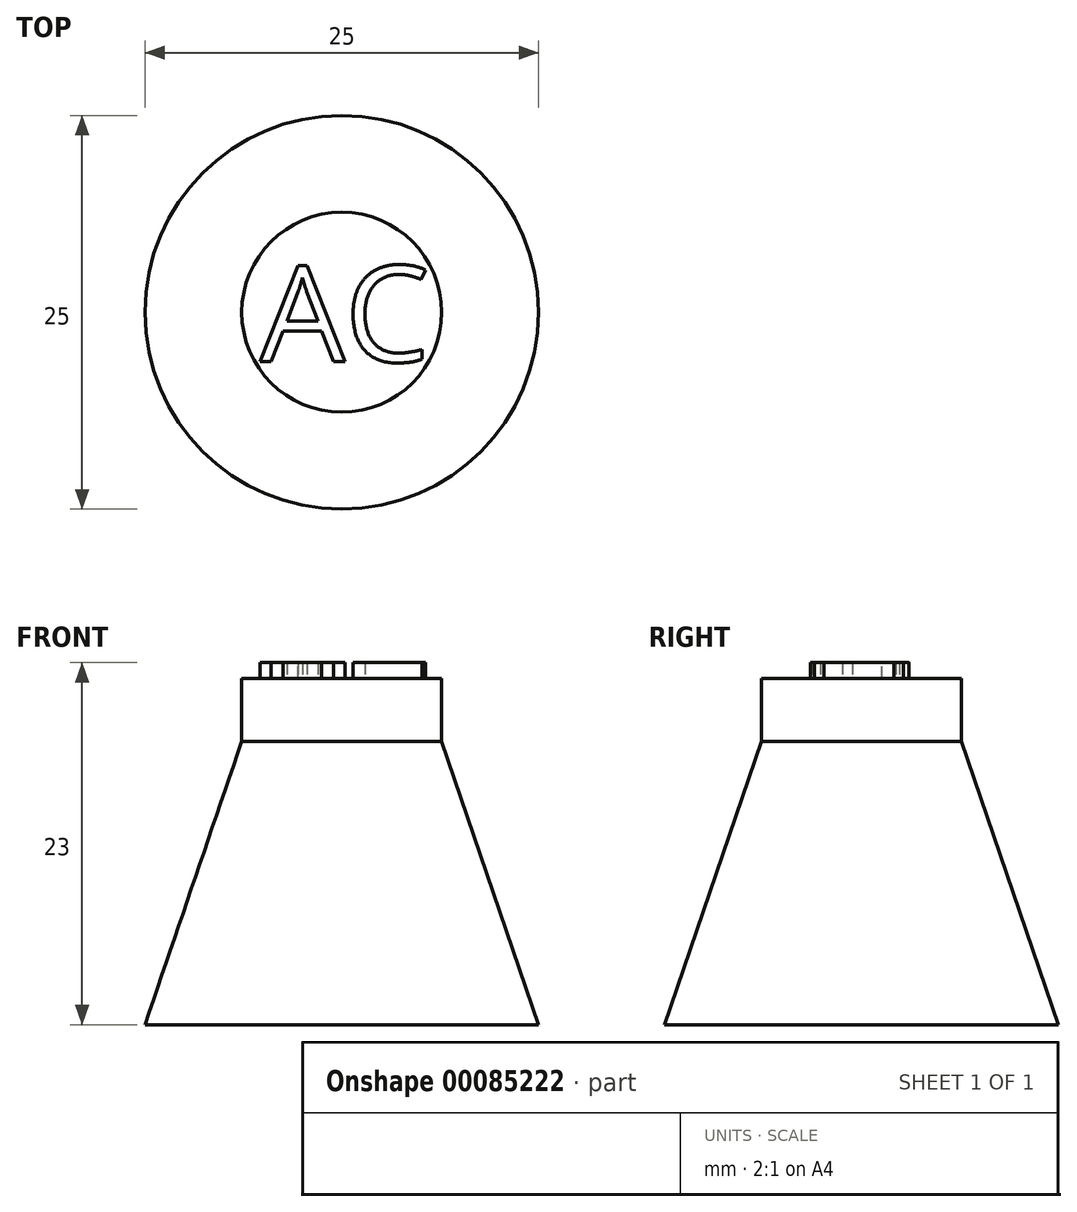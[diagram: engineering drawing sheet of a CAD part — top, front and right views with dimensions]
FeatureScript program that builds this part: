
annotation { "Feature Type Name" : "Feature", "Feature Type Description" : "" }
export const myFeature = defineFeature(function(context is Context, id is Id, definition is map)
    precondition{}
    {
        {
            var Q0;
            Q0=qCreatedBy(makeId("Front.planeOp"),FACE);
            var sketch = newSketch(context, id + "F0", { "sketchPlane" : qUnion([Q0])});
            skLineSegment(sketch, "E0", {"start": v(0, 0) * mm, "end": v(12.5, 0) * mm});
            skLineSegment(sketch, "E1", {"start": v(0, 0) * mm, "end": v(0, 18) * mm});
            skLineSegment(sketch, "E2", {"start": v(0, 18) * mm, "end": v(6.35, 18) * mm});
            skLineSegment(sketch, "E3", {"start": v(6.35, 18) * mm, "end": v(6.35, 22) * mm});
            skLineSegment(sketch, "E4", {"start": v(12.5, 0) * mm, "end": v(6.35, 18) * mm});
            skLineSegment(sketch, "E5", {"start": v(6.35, 22) * mm, "end": v(0, 22) * mm});
            skLineSegment(sketch, "E6", {"start": v(0, 22) * mm, "end": v(0, 18) * mm});
            skLineSegment(sketch, "E7", {"start": v(6.35, 18) * mm, "end": v(4.85, 18) * mm});
            skLineSegment(sketch, "E8", {"start": v(12.5, 0) * mm, "end": v(11, 0) * mm});
            skLineSegment(sketch, "E9", {"start": v(4.85, 18) * mm, "end": v(11, 0) * mm});
            skLineSegment(sketch, "E10", {"start": v(4.85, 18) * mm, "end": v(4.85, 22) * mm});
            skSolve(sketch);
        }
        {
            var Q0;
            Q0=makeQuery(id+"F0.imprint","IMPRINT",FACE,{"disambiguationData":[TD([[makeQuery(id+"F0.imprint","IMPRINT",EDGE,{"derivedFrom":sQuery(id+"F0.wireOp",EDGE,"E2")}),1.0]])]});
            var Q1;
            {var subQ0=sQuery(id+"F0.wireOp",EDGE,"E3");Q1=makeQuery(id+"F0.imprint","IMPRINT",FACE,{"disambiguationData":[TD([[makeQuery(id+"F0.imprint","IMPRINT",EDGE,{"derivedFrom":subQ0}),1.0]])]});}
            var Q2;
            Q2=makeQuery(id+"F0.imprint","IMPRINT",FACE,{"disambiguationData":[TD([[makeQuery(id+"F0.imprint","IMPRINT",EDGE,{"derivedFrom":sQuery(id+"F0.wireOp",EDGE,"E4")}),1.0]])]});
            var Q3;
            Q3=makeQuery(id+"F0.imprint","IMPRINT",FACE,{"disambiguationData":[TD([[makeQuery(id+"F0.imprint","IMPRINT",EDGE,{"derivedFrom":sQuery(id+"F0.wireOp",EDGE,"E0")}),1.0]])]});
            var Q4;
            Q4=sQuery(id+"F0.wireOp",EDGE,"E1");
            revolve(context, id + "F1", {"entities" : qUnion([Q0, Q1, Q2, Q3]), "axis" : qUnion([Q4]), "revolveType" : RevolveType.FULL});
        }
        {
            var Q0;
            Q0=makeQuery(id+"F1.opRevolve","SWEPT_FACE",FACE,{"disambiguationData":[OSD([sQuery(id+"F0.wireOp",EDGE,"E5")])]});
            var sketch = newSketch(context, id + "F2", { "sketchPlane" : qUnion([Q0])});
            skText(sketch, "E11", { "text": "AC", "fontName": "OpenSans-Regular.ttf"});
            const initialGuessF2  = {"E11": [-0.0052, -0.00314, 1, 0, 0.00614]};
            skSetInitialGuess(sketch, initialGuessF2);
            skSolve(sketch);
        }
        {
            var Q0;
            Q0=makeQuery(id+"F2.imprint","IMPRINT",FACE,{"disambiguationData":[TD([[makeQuery(id+"F2.imprint","IMPRINT",EDGE,{"derivedFrom":sQuery(id+"F2.wireOp",EDGE,"E11.sketch_text.stroke-0")}),-1.0]])]});
            var Q1;
            Q1=makeQuery(id+"F2.imprint","IMPRINT",FACE,{"disambiguationData":[TD([[makeQuery(id+"F2.imprint","IMPRINT",EDGE,{"derivedFrom":sQuery(id+"F2.wireOp",EDGE,"E11.sketch_text.stroke-13")}),-1.0]])]});
            extrude(context, id + "F3", {"entities" : qUnion([Q0, Q1]), "operationType" : NewBodyOperationType.ADD, "depth" : 1 * mm});
        }
    });
